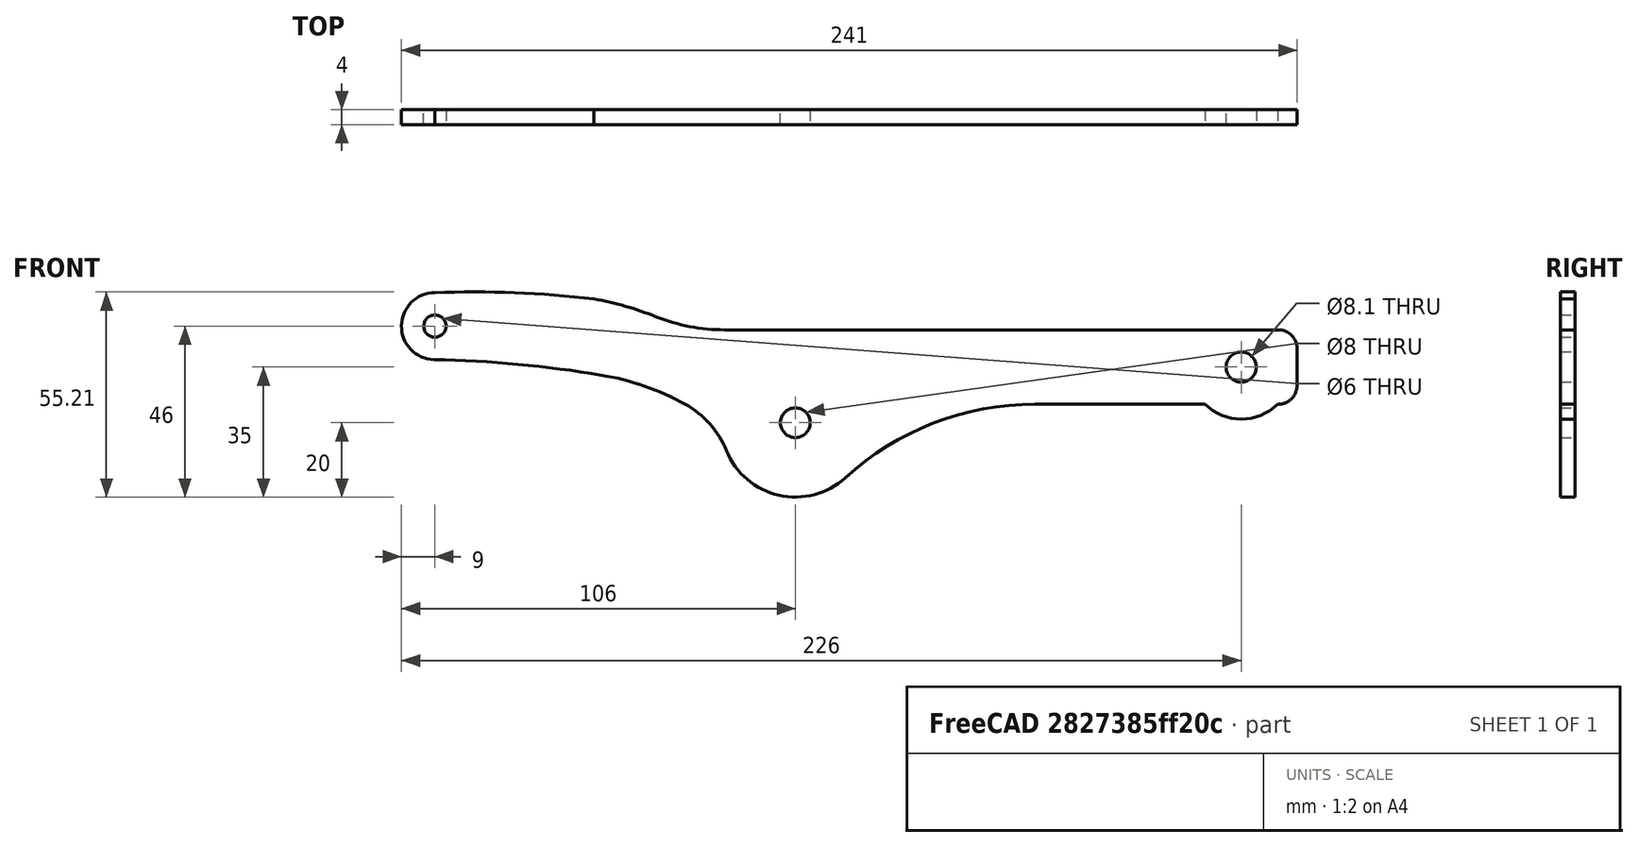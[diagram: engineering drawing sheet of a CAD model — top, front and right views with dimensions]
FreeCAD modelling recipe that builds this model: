
FCSTD DOCUMENT  (FreeCAD 0.19R19327 (Git))
Label: Balancinv2
License: All rights reserved
LicenseURL: http://en.wikipedia.org/wiki/All_rights_reserved
objects: Sketcher::SketchObject×1, PartDesign::Pad×1, PartDesign::Body×1
note: 4 computed .brp shape members not serialized (recipe doc carries the construction recipe); baked Part::Feature solids carry a one-line shape summary decoded from their .brp

FEATURE [Sketcher::SketchObject] Sketch
  MapMode = 5
  Placement = pos=(0,0,0) rot=(1,0,0;1.5708rad)
  Support = -> [XZ_Plane]
  sketch-geometry (19):
    g0: Circle CenterX=0 CenterY=0 CenterZ=0 NormalX=0 NormalY=0 NormalZ=1 AngleXU=0 Radius=4
    g1: ArcOfCircle CenterX=0 CenterY=0 CenterZ=0 NormalX=0 NormalY=0 NormalZ=1 AngleXU=0 Radius=20 StartAngle=3.52694 EndAngle=5.45203
    g2: LineSegment StartX=64.49 StartY=5 StartZ=0 EndX=110.202 EndY=5 EndZ=0
    g3: ArcOfCircle CenterX=64.49 CenterY=-70.6792 CenterZ=0 NormalX=0 NormalY=0 NormalZ=1 AngleXU=0 Radius=75.6792 StartAngle=1.5708 EndAngle=2.31044
    g4: ArcOfCircle CenterX=-41.7 CenterY=-16.9148 CenterZ=0 NormalX=0 NormalY=0 NormalZ=1 AngleXU=0 Radius=25 StartAngle=0.385351 EndAngle=1.06785
    g5: ArcOfCircle CenterX=-63.8724 CenterY=-57.2185 CenterZ=0 NormalX=0 NormalY=0 NormalZ=1 AngleXU=0 Radius=71 StartAngle=1.06785 EndAngle=1.4058
    g6: Circle CenterX=-97 CenterY=26 CenterZ=0 NormalX=0 NormalY=0 NormalZ=1 AngleXU=0 Radius=3
    g7: ArcOfCircle CenterX=-97 CenterY=26 CenterZ=0 NormalX=0 NormalY=0 NormalZ=1 AngleXU=0 Radius=9 StartAngle=1.5708 EndAngle=4.69183
    g8: Circle CenterX=120 CenterY=15 CenterZ=0 NormalX=0 NormalY=0 NormalZ=1 AngleXU=0 Radius=4.05
    g9: LineSegment StartX=130 StartY=25 StartZ=0 EndX=-19 EndY=25 EndZ=0
    g10: ArcOfCircle CenterX=-103.62 CenterY=-295.932 CenterZ=0 NormalX=0 NormalY=0 NormalZ=1 AngleXU=0 Radius=313 StartAngle=1.4058 EndAngle=1.55024
    g11: LineSegment StartX=135 StartY=20 StartZ=0 EndX=135 EndY=10 EndZ=0
    g12: ArcOfCircle CenterX=130 CenterY=20 CenterZ=0 NormalX=0 NormalY=0 NormalZ=1 AngleXU=0 Radius=5 StartAngle=0 EndAngle=1.5708
    g13: ArcOfCircle CenterX=120 CenterY=15 CenterZ=0 NormalX=0 NormalY=0 NormalZ=1 AngleXU=0 Radius=14 StartAngle=3.9372 EndAngle=5.48798
    g14: ArcOfCircle CenterX=130 CenterY=10 CenterZ=0 NormalX=0 NormalY=0 NormalZ=1 AngleXU=0 Radius=5 StartAngle=4.67277 EndAngle=6.28319
    g15: ArcOfCircle CenterX=-19 CenterY=75 CenterZ=0 NormalX=0 NormalY=0 NormalZ=1 AngleXU=0 Radius=50 StartAngle=4.33298 EndAngle=4.71239
    g16: ArcOfCircle CenterX=-69 CenterY=-50.3994 CenterZ=0 NormalX=0 NormalY=0 NormalZ=1 AngleXU=0 Radius=85 StartAngle=1.19139 EndAngle=1.39537
    g17: ArcOfCircle CenterX=-86.4 CenterY=-237.794 CenterZ=0 NormalX=0 NormalY=0 NormalZ=1 AngleXU=0 Radius=273 StartAngle=1.45244 EndAngle=1.60963
    g18: LineSegment [constr] StartX=-97 StartY=26 StartZ=0 EndX=-97 EndY=35 EndZ=0
  constraints (54):
    c: Coincident(g0,g-1)
    c: Radius(g0) = 4
    c: Coincident(g1,g0)
    c: Radius(g1) = 20
    c: Horizontal(g2)
    c: Tangent(g3,g2) = 1.5708
    c: Radius(g4) = 25
    c: Radius(g5) = 71
    c: DistanceX(g4,g0) = 41.7
    c: Tangent(g4,g1) = 1.5708
    c: Tangent(g4,g5) = -1.5708
    c: Radius(g6) = 3
    c: DistanceX(g6,g0) = 97
    c: DistanceY(g0,g6) = 26
    c: Coincident(g7,g6)
    c: Radius(g7) = 9
    c: Radius(g8) = 4.05
    c: DistanceX(g0,g8) = 120
    c: DistanceY(g0,g8) = 15
    c: Horizontal(g9)
    c: Radius(g10) = 313
    c: Tangent(g5,g10) = -1.5708
    c: Vertical(g11)
    c: DistanceX(g8,g11) = 15
    c: Tangent(g11,g12) = 1.5708
    c: Tangent(g9,g12) = -1.5708
    c: Coincident(g13,g8)
    c: Radius(g13) = 14
    c: Coincident(g2,g13)
    c: Radius(g12) = 5
    c: DistanceY(g8,g9) = 10
    c: DistanceY(g11,g11) = 10
    c: Tangent(g14,g11) = 1.5708
    c: Equal(g14,g12)
    c: Coincident(g13,g14)
    c: Coincident(g15,g9)
    c: Radius(g15) = 50
    c: DistanceX(g9,g9) = 149
    c: DistanceY(g0,g15) = 75
    c: Radius(g16) = 85
    c: DistanceX(g16,g0) = 69
    c: Radius(g17) = 273
    c: DistanceX(g17,g0) = 86.4
    c: Coincident(g17,g16)
    c: Coincident(g7,g17)
    c: Coincident(g18,g6)
    c: Vertical(g18)
    c: Coincident(g18,g7)
    c: DistanceY(g2,g8) = 10
    c: Tangent(g3,g1) = 1.5708
    c: DistanceX(g10,g0) = 103.62
    c: DistanceX(g0,g3) = 64.49
    c: Tangent(g10,g7) = 1.5708
    c: Tangent(g15,g16) = 1.5708
FEATURE [PartDesign::Pad] Pad
  Length = 4
  Length2 = 100
  Placement = pos=(0,0,0) rot=(1,0,0;1.5708rad)
  Profile = -> Sketch
  Type = 0
FEATURE [PartDesign::Body] Body
  Group = -> [Sketch,Pad]
  Origin = -> Origin
  Tip = -> Pad
